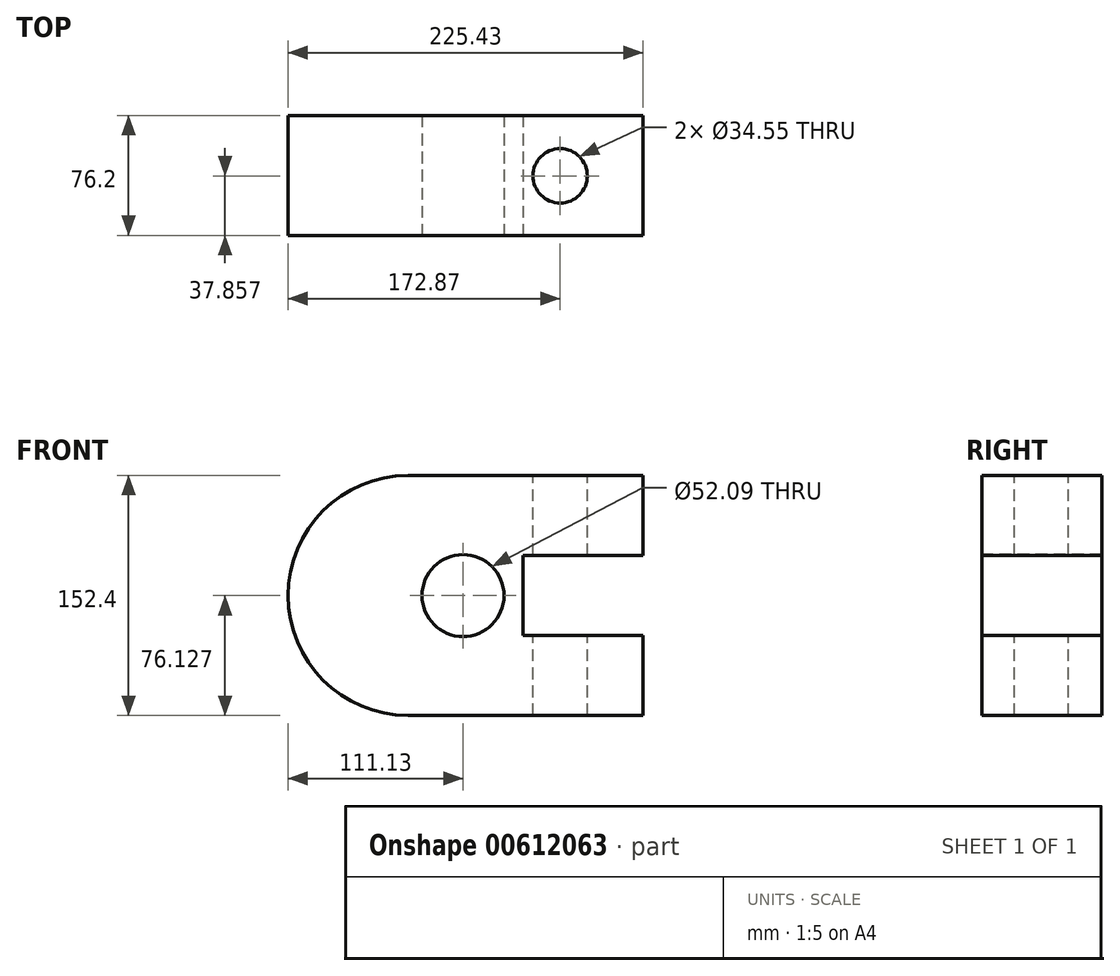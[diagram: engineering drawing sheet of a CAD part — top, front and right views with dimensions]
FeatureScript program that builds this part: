
annotation { "Feature Type Name" : "Feature", "Feature Type Description" : "" }
export const myFeature = defineFeature(function(context is Context, id is Id, definition is map)
    precondition{}
    {
        {
            var Q0;
            Q0=qCreatedBy(makeId("Front.planeOp"),FACE);
            var sketch = newSketch(context, id + "F0", { "sketchPlane" : qUnion([Q0])});
            skLineSegment(sketch, "E0", {"start": v(0, 0) * mm, "end": v(0, 50.8) * mm});
            skLineSegment(sketch, "E1", {"start": v(0, 50.8) * mm, "end": v(-149.23, 50.8) * mm});
            skLineSegment(sketch, "E2", {"start": v(0, 0) * mm, "end": v(-76.2, 0) * mm});
            skLineSegment(sketch, "E3", {"start": v(-76.2, 0) * mm, "end": v(-76.2, -50.8) * mm});
            skLineSegment(sketch, "E4", {"start": v(-76.2, -50.8) * mm, "end": v(0, -50.8) * mm});
            skLineSegment(sketch, "E5", {"start": v(0, -50.8) * mm, "end": v(0, -101.6) * mm});
            skLineSegment(sketch, "E6", {"start": v(0, -101.6) * mm, "end": v(-149.23, -101.6) * mm});
            skArc(sketch, "E7", {"start": v(-149.23, 50.8) * mm, "mid": v(-225.43, -25.4) * mm, "end": v(-149.23, -101.6) * mm});
            skPoint(sketch, "E8", {"position": v(-76.2, -25.4) * mm});
            skCircle(sketch, "E9", {"center": v(-114.3, -25.47) * mm, "radius": 26.04 * mm});
            skSolve(sketch);
        }
        {
            var Q0;
            Q0=makeQuery(id+"F0.imprint","IMPRINT",FACE,{"disambiguationData":[TD([[makeQuery(id+"F0.imprint","IMPRINT",EDGE,{"derivedFrom":sQuery(id+"F0.wireOp",EDGE,"E0")}),1.0]])]});
            extrude(context, id + "F1", {"entities" : qUnion([Q0]), "oppositeDirection" : true, "depth" : 76.2 * mm, "offsetDistance" : 25.4 * mm});
        }
        {
            var Q0;
            Q0=makeQuery(id+"F1.opExtrude","SWEPT_FACE",FACE,{"disambiguationData":[OSD([sQuery(id+"F0.wireOp",EDGE,"E1")])]});
            var sketch = newSketch(context, id + "F2", { "sketchPlane" : qUnion([Q0])});
            skCircle(sketch, "E10", {"center": v(-52.56, 37.86) * mm, "radius": 17.27 * mm});
            skSolve(sketch);
        }
        {
            var Q0;
            Q0=makeQuery(id+"F2.imprint","IMPRINT",FACE,{"disambiguationData":[TD([[makeQuery(id+"F2.imprint","IMPRINT",EDGE,{"derivedFrom":sQuery(id+"F2.wireOp",EDGE,"E10")}),1.0]])]});
            extrude(context, id + "F3", {"entities" : qUnion([Q0]), "operationType" : NewBodyOperationType.REMOVE, "oppositeDirection" : true, "depth" : 152.4 * mm, "offsetDistance" : 25.4 * mm});
        }
    });
